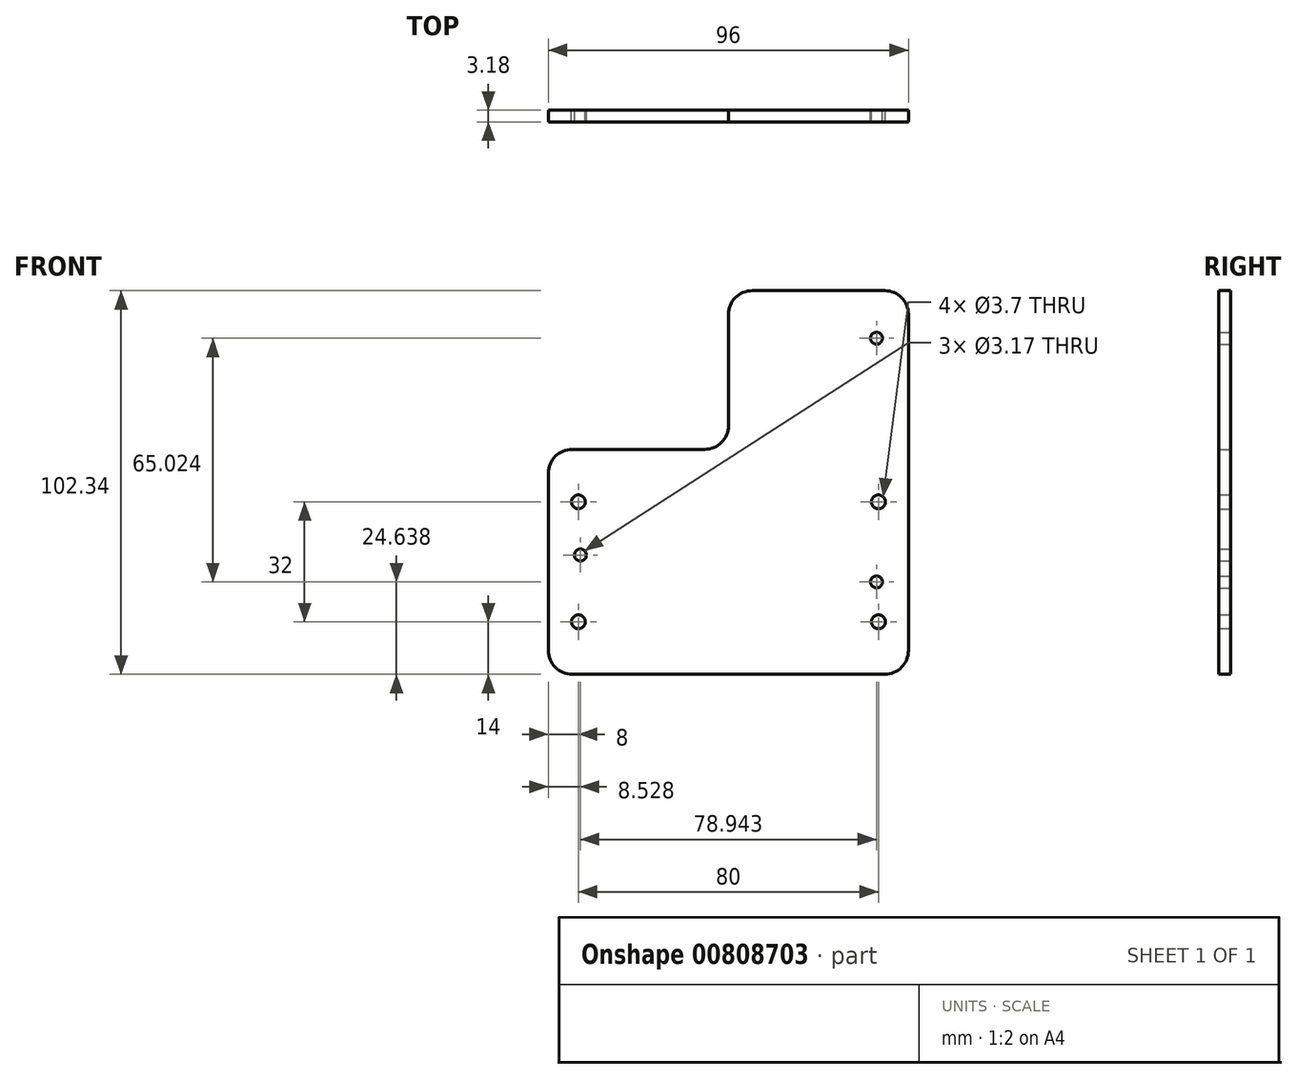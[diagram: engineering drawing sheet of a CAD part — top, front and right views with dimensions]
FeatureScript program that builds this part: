
annotation { "Feature Type Name" : "Feature", "Feature Type Description" : "" }
export const myFeature = defineFeature(function(context is Context, id is Id, definition is map)
    precondition{}
    {
        {
            var Q0;
            Q0=qCreatedBy(makeId("Front.planeOp"),FACE);
            var sketch = newSketch(context, id + "F0", { "sketchPlane" : qUnion([Q0])});
            skCircle(sketch, "E0", {"center": v(40, 16) * mm, "radius": 1.85 * mm});
            skCircle(sketch, "E1.MirrorC", {"center": v(-40, 16) * mm, "radius": 1.85 * mm});
            skCircle(sketch, "E2.MirrorC", {"center": v(40, -16) * mm, "radius": 1.85 * mm});
            skCircle(sketch, "E3.MirrorC", {"center": v(-40, -16) * mm, "radius": 1.85 * mm});
            skLineSegment(sketch, "E4.bottom", {"start": v(-41.65, -30) * mm, "end": v(41.65, -30) * mm});
            skLineSegment(sketch, "E4.top", {"start": v(-41.65, 30) * mm, "end": v(-6.35, 30) * mm});
            skLineSegment(sketch, "E4.left", {"start": v(-48, -23.65) * mm, "end": v(-48, 23.65) * mm});
            skLineSegment(sketch, "E4.right", {"start": v(48, -23.65) * mm, "end": v(48, 30) * mm});
            skLineSegment(sketch, "E5.top", {"start": v(41.65, 72.34) * mm, "end": v(6.35, 72.34) * mm});
            skLineSegment(sketch, "E5.left", {"start": v(48, 30) * mm, "end": v(48, 66) * mm});
            skLineSegment(sketch, "E5.right", {"start": v(0, 36.35) * mm, "end": v(0, 66) * mm});
            skPoint(sketch, "E6.visualSharp", {"position": v(-48, -30) * mm});
            skArc(sketch, "E6.filletArc", {"start": v(-48, -23.65) * mm, "mid": v(-46.14, -28.14) * mm, "end": v(-41.65, -30) * mm});
            skPoint(sketch, "E7.visualSharp", {"position": v(48, -30) * mm});
            skArc(sketch, "E7.filletArc", {"start": v(41.65, -30) * mm, "mid": v(46.14, -28.14) * mm, "end": v(48, -23.65) * mm});
            skPoint(sketch, "E8.visualSharp", {"position": v(48, 72.34) * mm});
            skArc(sketch, "E8.filletArc", {"start": v(48, 66) * mm, "mid": v(46.14, 70.48) * mm, "end": v(41.65, 72.34) * mm});
            skPoint(sketch, "E9.visualSharp", {"position": v(0, 72.34) * mm});
            skArc(sketch, "E9.filletArc", {"start": v(6.35, 72.34) * mm, "mid": v(1.86, 70.48) * mm, "end": v(0, 66) * mm});
            skPoint(sketch, "E10.newPointB", {"position": v(-48, 27.15) * mm});
            skArc(sketch, "E10.filletArc", {"start": v(-41.65, 30) * mm, "mid": v(-46.14, 28.14) * mm, "end": v(-48, 23.65) * mm});
            skPoint(sketch, "E11.newPointA", {"position": v(48, 30) * mm});
            skArc(sketch, "E11.filletArc", {"start": v(-6.35, 30) * mm, "mid": v(-1.86, 31.86) * mm, "end": v(0, 36.35) * mm});
            skCircle(sketch, "E12", {"center": v(-39.47, 1.83) * mm, "radius": 1.59 * mm});
            skCircle(sketch, "E13", {"center": v(39.47, -5.36) * mm, "radius": 1.59 * mm});
            skCircle(sketch, "E14", {"center": v(39.47, 59.66) * mm, "radius": 1.59 * mm});
            skPoint(sketch, "E15.start.orphan", {"position": v(0, 27.15) * mm});
            skPoint(sketch, "E16.trimOffspring.end.orphan", {"position": v(0, 30) * mm});
            skPoint(sketch, "E17.MirrorCS.start.orphan", {"position": v(0, 0) * mm});
            skPoint(sketch, "E18.orphan", {"position": v(48, 0) * mm});
            skPoint(sketch, "E19.end.orphan", {"position": v(-48, 0) * mm});
            skPoint(sketch, "E20.end.orphan", {"position": v(0, -30) * mm});
            skSolve(sketch);
        }
        {
            var Q0;
            Q0=makeQuery(id+"F0.imprint","IMPRINT",FACE,{"disambiguationData":[TD([[makeQuery(id+"F0.imprint","IMPRINT",EDGE,{"derivedFrom":sQuery(id+"F0.wireOp",EDGE,"E0")}),-1.0]])]});
            extrude(context, id + "F1", {"entities" : qUnion([Q0]), "depth" : 3.17 * mm, "offsetDistance" : 25.4 * mm});
        }
    });
